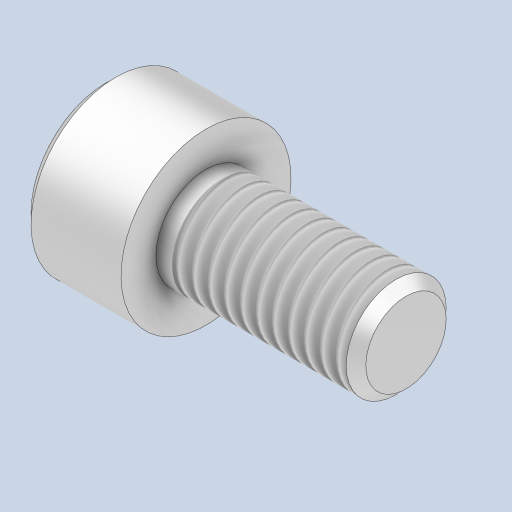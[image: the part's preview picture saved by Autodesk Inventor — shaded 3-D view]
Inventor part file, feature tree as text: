
AUTODESK INVENTOR PART (.ipt)
format: ipt  version: 2023 (Build 270158000, 158)  size: 206,848 bytes
history: native  units: mm
features: other x14, sketch x3, revolve x1, thread x1, hole x1, extrude x1
ambient origin geometry x8: Origin, YZ Plane, XZ Plane, XY Plane, X Axis, Y Axis, Z Axis, Center Point
bodies: Solid1 (feature_tree)
feature tree (21):
  revolve  "Revolution1"  [1 undecoded]
  thread  "Thread1"  [1 undecoded]
  hole  "Hole1"  [1 undecoded]
  extrude  "Extrusion1"  [1 undecoded]
  other  "bolt_XY"
  other  "bolt_YZ"
  other  "bolt_ZX"
  other  "bolt_X"
  other  "bolt_Y"
  other  "bolt_Z"
  other  "bolt_Center"
  other  "nut_XY"
  other  "nut_YZ"
  other  "nut_ZX"
  other  "nut_X"
  other  "nut_Y"
  other  "nut_Z"
  other  "nut_Center"
  sketch  "Sketch_1"  dims[d0=360.0deg d1=8.7095mm d2=0.0mm]
  sketch  "Sketch2"  dims[d3=4.0mm d4=6.0mm d5=4.0mm d6=2.0mm d7=90.0deg d8=2.5mm d9=150.0deg d10=2.5mm d11=0.0mm]
  sketch  "Sketch_3"  dims[d12=0.0mm d13=0.0mm]
note: 4 required parameter values undecoded (feature->parameter linkage not recoverable at this tier; creation-order binding heuristic only, values carry confidence <= 0.55)